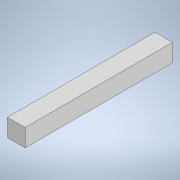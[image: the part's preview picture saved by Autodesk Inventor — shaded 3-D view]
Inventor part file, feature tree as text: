
AUTODESK INVENTOR PART (.ipt)
format: ipt  version: 2020.1 (Build 241239000, 239)  size: 92,672 bytes
history: native  units: in
note: dims shown in document units (in); Inventor stores cm internally (conversion verified against a paired STEP export)
features: extrude x1, sketch x1
ambient origin geometry x8: Origin, YZ Plane, XZ Plane, XY Plane, X Axis, Y Axis, Z Axis, Center Point
bodies: Solid1 (feature_tree)
feature tree (2):
  extrude  "Extrusion1"  Depth=0.2362in
  sketch  "Sketch1"  dims[d0=0.2362in d1=0.2362in d2=1.9685in d3=0.0in]
